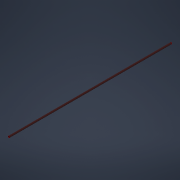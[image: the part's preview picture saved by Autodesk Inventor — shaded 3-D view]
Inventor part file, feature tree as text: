
AUTODESK INVENTOR PART (.ipt)
format: ipt  version: 2022 (Build 260153000, 153)  size: 103,936 bytes
history: native  units: mm
features: extrude x1, sketch x1
ambient origin geometry x8: Origin, YZ Plane, XZ Plane, XY Plane, X Axis, Y Axis, Z Axis, Center Point
bodies: Solid1 (feature_tree)
feature tree (2):
  extrude  "Extrusion1"  Depth=4550.0mm TaperAngle=0.0deg
  sketch  "Sketch1"  dims[d0=45.0mm d1=4550.0mm d2=0.0mm d3=0.5mm d4=0.872665mm d5=0.5mm d6=0.872665mm]
